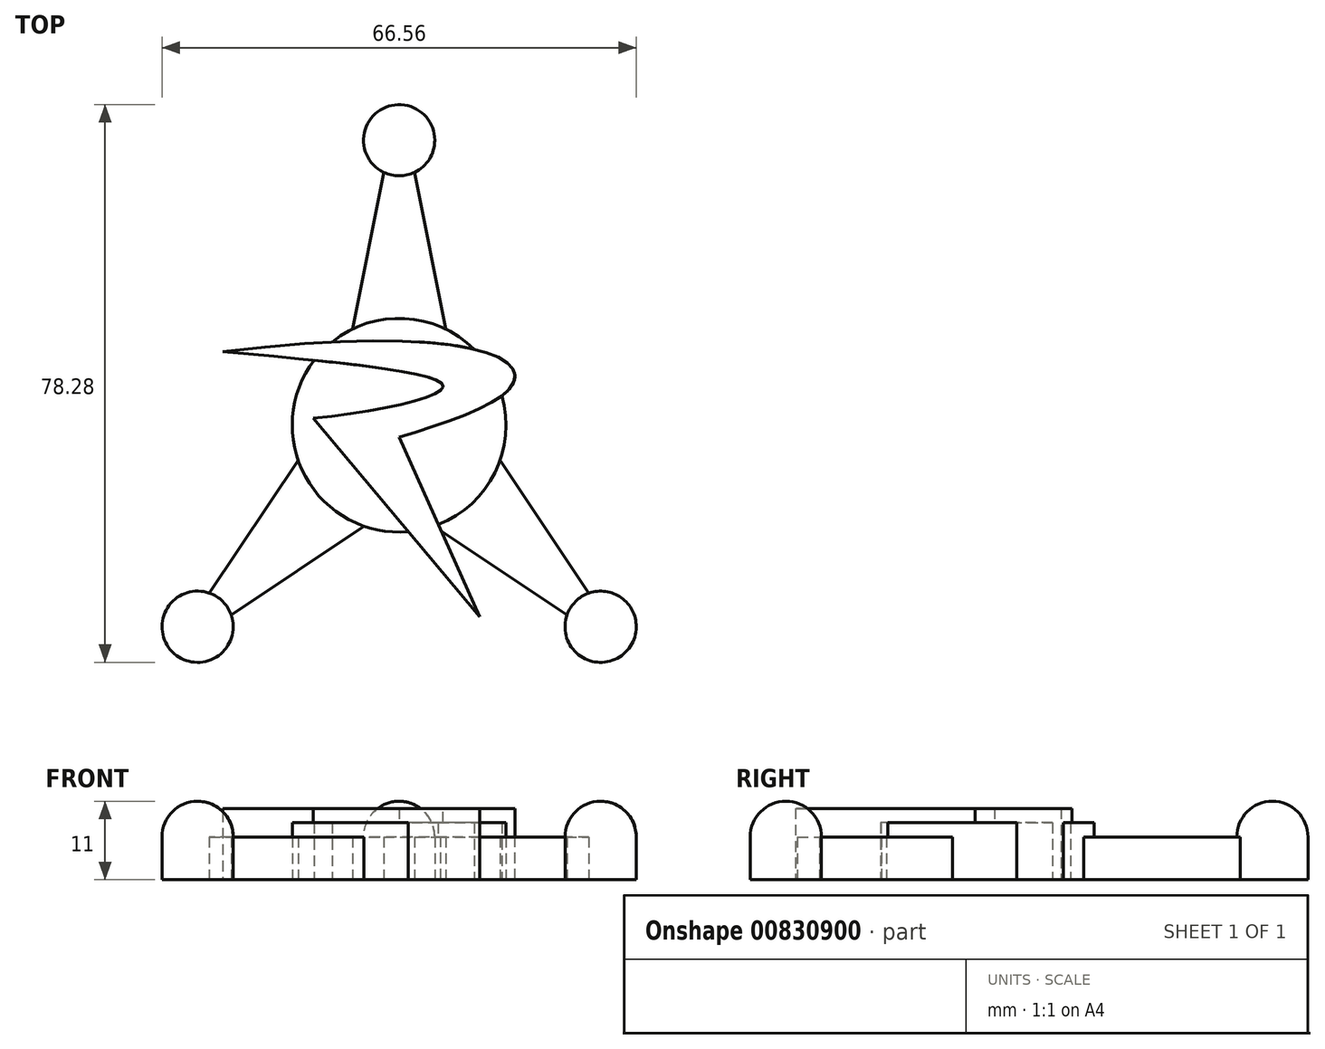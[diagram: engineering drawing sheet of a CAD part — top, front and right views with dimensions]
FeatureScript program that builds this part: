
annotation { "Feature Type Name" : "Feature", "Feature Type Description" : "" }
export const myFeature = defineFeature(function(context is Context, id is Id, definition is map)
    precondition{}
    {
        {
            var Q0;
            Q0=qCreatedBy(makeId("Top.planeOp"),FACE);
            var sketch = newSketch(context, id + "F0", { "sketchPlane" : qUnion([Q0])});
            skCircle(sketch, "E0", {"center": v(0, 0) * mm, "radius": 15 * mm});
            skLineSegment(sketch, "E1", {"start": v(0, 15) * mm, "end": v(0, 40) * mm});
            skCircle(sketch, "E2", {"center": v(0, 40) * mm, "radius": 5 * mm});
            skLineSegment(sketch, "E3", {"start": v(2.18, 35.5) * mm, "end": v(6.54, 13.5) * mm});
            skLineSegment(sketch, "E4", {"start": v(-6.54, 13.5) * mm, "end": v(-2.18, 35.5) * mm});
            skCircle(sketch, "E5", {"center": v(-28.28, -28.28) * mm, "radius": 5 * mm});
            skCircle(sketch, "E6", {"center": v(28.28, -28.28) * mm, "radius": 5 * mm});
            skLineSegment(sketch, "E7", {"start": v(0, 0) * mm, "end": v(0, 13.5) * mm});
            skLineSegment(sketch, "E8", {"start": v(0, 13.5) * mm, "end": v(-6.54, 13.5) * mm});
            skLineSegment(sketch, "E9", {"start": v(-26.64, -23.56) * mm, "end": v(-14.17, -4.92) * mm});
            skLineSegment(sketch, "E10", {"start": v(-23.56, -26.64) * mm, "end": v(-4.92, -14.17) * mm});
            skLineSegment(sketch, "E11", {"start": v(23.56, -26.64) * mm, "end": v(4.92, -14.17) * mm});
            skLineSegment(sketch, "E12", {"start": v(14.17, -4.92) * mm, "end": v(26.64, -23.56) * mm});
            skSolve(sketch);
        }
        {
            var Q0;
            Q0 = qSketchRegion(id + "F0", true);
            extrude(context, id + "F1", {"entities" : qUnion([Q0]), "depth" : 6 * mm, "offsetDistance" : 25 * mm});
        }
        {
            var Q0;
            Q0=qCreatedBy(makeId("Top.planeOp"),FACE);
            var sketch = newSketch(context, id + "F2", { "sketchPlane" : qUnion([Q0])});
            skCircle(sketch, "E13", {"center": v(0, 40) * mm, "radius": 5 * mm});
            skCircle(sketch, "E14", {"center": v(-28.28, -28.28) * mm, "radius": 5 * mm});
            skCircle(sketch, "E15", {"center": v(28.28, -28.28) * mm, "radius": 5 * mm});
            skSolve(sketch);
        }
        {
            var Q0;
            Q0 = qSketchRegion(id + "F2", true);
            extrude(context, id + "F3", {"entities" : qUnion([Q0]), "operationType" : NewBodyOperationType.ADD, "depth" : 11 * mm, "offsetDistance" : 25 * mm});
        }
        {
            var Q0;
            Q0=makeQuery(id+"F3.opExtrude","CAP_EDGE",EDGE,{"disambiguationData":[OSD([sQuery(id+"F2.wireOp",EDGE,"E13")])],"isStart":false});
            var Q1;
            Q1=makeQuery(id+"F3.opExtrude","CAP_EDGE",EDGE,{"disambiguationData":[OSD([sQuery(id+"F2.wireOp",EDGE,"E15")])],"isStart":false});
            var Q2;
            Q2=makeQuery(id+"F3.opExtrude","CAP_EDGE",EDGE,{"disambiguationData":[OSD([sQuery(id+"F2.wireOp",EDGE,"E14")])],"isStart":false});
            fillet(context, id + "F4", {"entities" : qUnion([Q0, Q1, Q2]), "radius" : 5 * mm, "tangentPropagation" : true, "allowEdgeOverflow" : false});
        }
        {
            var Q0;
            Q0=makeQuery(id+"F1.opExtrude","CAP_FACE",FACE,{"disambiguationData":[OSD([sQuery(id+"F0.wireOp",EDGE,"E0"),sQuery(id+"F0.wireOp",EDGE,"E2"),sQuery(id+"F0.wireOp",EDGE,"E3"),sQuery(id+"F0.wireOp",EDGE,"E4"),sQuery(id+"F0.wireOp",EDGE,"E5"),sQuery(id+"F0.wireOp",EDGE,"E6"),sQuery(id+"F0.wireOp",EDGE,"E9"),sQuery(id+"F0.wireOp",EDGE,"E10"),sQuery(id+"F0.wireOp",EDGE,"E11"),sQuery(id+"F0.wireOp",EDGE,"E12")])],"isStart":false});
            var sketch = newSketch(context, id + "F5", { "sketchPlane" : qUnion([Q0])});
            skCircle(sketch, "E16", {"center": v(0, 0) * mm, "radius": 15 * mm});
            skSolve(sketch);
        }
        {
            var Q0;
            Q0 = qSketchRegion(id + "F5", true);
            extrude(context, id + "F6", {"entities" : qUnion([Q0]), "operationType" : NewBodyOperationType.ADD, "depth" : 2 * mm, "offsetDistance" : 25 * mm});
        }
        {
            var Q0;
            Q0=qCreatedBy(makeId("Top.planeOp"),FACE);
            var sketch = newSketch(context, id + "F7", { "sketchPlane" : qUnion([Q0])});
            skFitSpline(sketch, "E17", {"points": [v(-24.79, 10.32) * mm, v(15.94, 7.93) * mm, v(15.07, 4.69) * mm, v(0, -1.69) * mm], "startDerivative": vector(142.8, 17.74) * mm, "endDerivative": vector(-54.26, -16.83) * mm});
            skLineSegment(sketch, "E18", {"start": v(0, -1.69) * mm, "end": v(11.29, -26.91) * mm});
            skLineSegment(sketch, "E19", {"start": v(11.29, -26.91) * mm, "end": v(-12.04, 1) * mm});
            skFitSpline(sketch, "E20", {"points": [v(-12.04, 1) * mm, v(6.17, 5.42) * mm, v(-24.79, 10.32) * mm], "startDerivative": vector(59.61, 5.38) * mm, "endDerivative": vector(-83.84, 7.5) * mm});
            skSolve(sketch);
        }
        {
            var Q0;
            Q0=makeQuery(id+"F7.imprint","IMPRINT",FACE,{"disambiguationData":[TD([[makeQuery(id+"F7.imprint","IMPRINT",EDGE,{"derivedFrom":sQuery(id+"F7.wireOp",EDGE,"E17")}),-1.0]])]});
            extrude(context, id + "F8", {"entities" : qUnion([Q0]), "operationType" : NewBodyOperationType.ADD, "depth" : 10 * mm, "offsetDistance" : 25 * mm});
        }
    });
